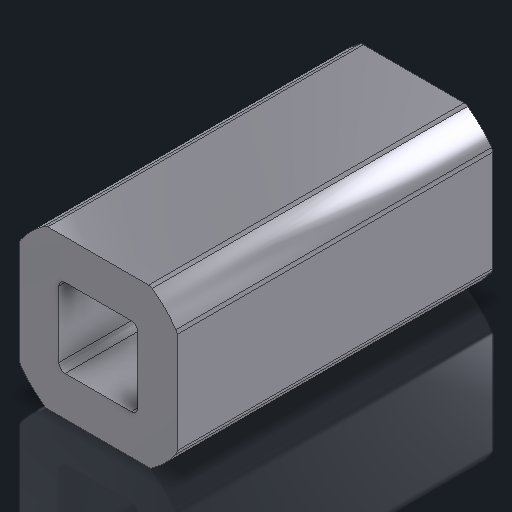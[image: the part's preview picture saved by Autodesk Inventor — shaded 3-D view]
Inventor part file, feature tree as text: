
AUTODESK INVENTOR PART (.ipt)
format: ipt  version: 2023.2 (Build 272271030, 271C)  size: 181,760 bytes
history: native  units: in
note: dims shown in document units (in); Inventor stores cm internally (conversion verified against a paired STEP export)
features: extrude x2, sketch x2, fillet x1
ambient origin geometry x8: Origin, YZ Plane, XZ Plane, XY Plane, X Axis, Y Axis, Z Axis, Center Point
bodies: Solid1 (feature_tree)
feature tree (5):
  extrude  "Extrusion1"  Depth=0.25in
  extrude  "Extrusion2"  Depth=0.5in TaperAngle=0.0deg
  fillet  "Fillet1"  Radius=0.125in
  sketch  "Sketch1"  dims[d0=0.3in d1=0.25in]
  sketch  "Sketch2"  dims[d2=0.5in d3=0.0in d5=0.5in d6=0.0in d7=0.125in d8=0.01in]
